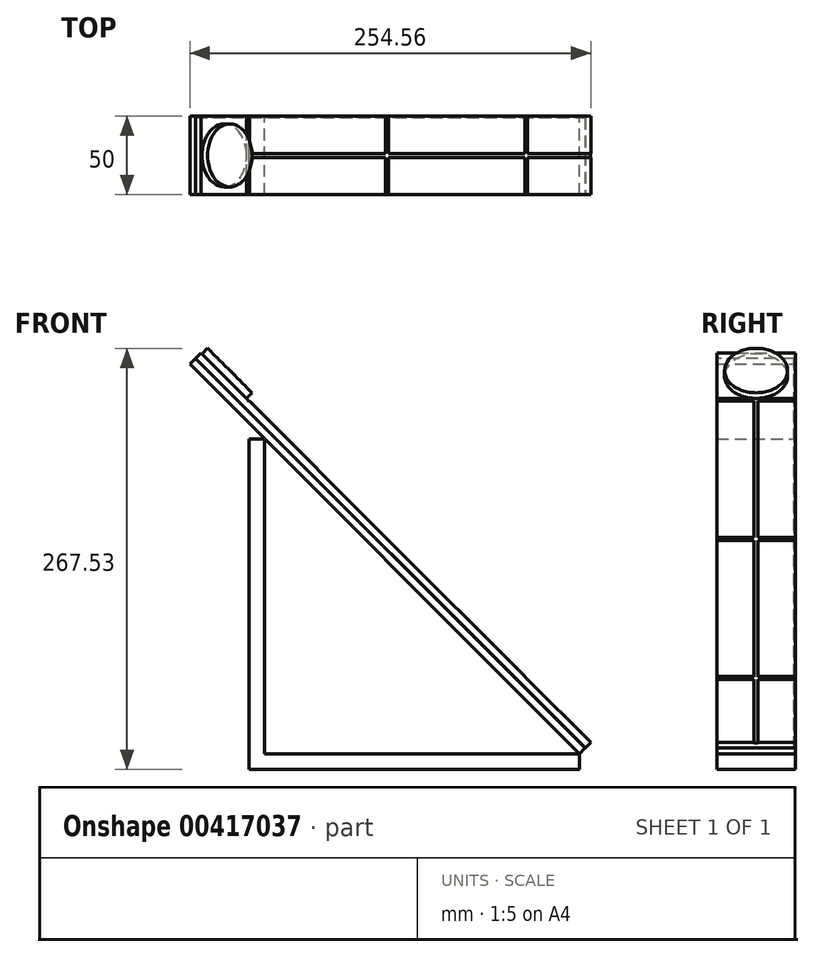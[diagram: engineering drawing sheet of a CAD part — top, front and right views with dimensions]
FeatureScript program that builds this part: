
annotation { "Feature Type Name" : "Feature", "Feature Type Description" : "" }
export const myFeature = defineFeature(function(context is Context, id is Id, definition is map)
    precondition{}
    {
        {
            var Q0;
            Q0=qCreatedBy(makeId("Top.planeOp"),FACE);
            var sketch = newSketch(context, id + "F0", { "sketchPlane" : qUnion([Q0])});
            skLineSegment(sketch, "E0.bottom", {"start": v(-52.98, -30.4) * mm, "end": v(147.02, -30.4) * mm});
            skLineSegment(sketch, "E0.top", {"start": v(-52.98, 19.6) * mm, "end": v(147.02, 19.6) * mm});
            skLineSegment(sketch, "E0.left", {"start": v(-52.98, -30.4) * mm, "end": v(-52.98, 19.6) * mm});
            skLineSegment(sketch, "E0.right", {"start": v(147.02, -30.4) * mm, "end": v(147.02, 19.6) * mm});
            skSolve(sketch);
        }
        {
            var Q0;
            Q0=makeQuery(id+"F0.imprint","IMPRINT",FACE,{"disambiguationData":[TD([[makeQuery(id+"F0.imprint","IMPRINT",EDGE,{"derivedFrom":sQuery(id+"F0.wireOp",EDGE,"E0.bottom")}),1.0]])]});
            extrude(context, id + "F1", {"entities" : qUnion([Q0]), "depth" : 200 * mm});
        }
        {
            var Q0;
            Q0=makeQuery(id+"F1.opExtrude","SWEPT_FACE",FACE,{"disambiguationData":[OSD([sQuery(id+"F0.wireOp",EDGE,"E0.bottom")])]});
            var sketch = newSketch(context, id + "F2", { "sketchPlane" : qUnion([Q0])});
            skLineSegment(sketch, "E1", {"start": v(-52.98, 200) * mm, "end": v(147.02, 0) * mm});
            skLineSegment(sketch, "E2", {"start": v(147.02, 0) * mm, "end": v(147.02, 200) * mm});
            skLineSegment(sketch, "E3", {"start": v(147.02, 200) * mm, "end": v(-52.98, 200) * mm});
            skSolve(sketch);
        }
        {
            var Q0;
            Q0=makeQuery(id+"F2.imprint","IMPRINT",FACE,{"disambiguationData":[TD([[makeQuery(id+"F2.imprint","IMPRINT",EDGE,{"derivedFrom":sQuery(id+"F2.wireOp",EDGE,"E1")}),1.0]])]});
            extrude(context, id + "F3", {"entities" : qUnion([Q0]), "operationType" : NewBodyOperationType.REMOVE, "oppositeDirection" : true, "depth" : 209 * mm});
        }
        {
            var Q0;
            Q0=makeQuery(id+"F3.boolean.opBoolean","COPY",FACE,{"derivedFrom":makeQuery(id+"F3.opExtrude","SWEPT_FACE",FACE,{"disambiguationData":[OSD([sQuery(id+"F2.wireOp",EDGE,"E1")])]})});
            var sketch = newSketch(context, id + "F4", { "sketchPlane" : qUnion([Q0])});
            skLineSegment(sketch, "E4.bottom", {"start": v(-30.4, -103.96) * mm, "end": v(19.6, -103.96) * mm});
            skLineSegment(sketch, "E4.top", {"start": v(-30.4, 246.04) * mm, "end": v(19.6, 246.04) * mm});
            skLineSegment(sketch, "E4.left", {"start": v(-30.4, -103.96) * mm, "end": v(-30.4, 246.04) * mm});
            skLineSegment(sketch, "E4.right", {"start": v(19.6, -103.96) * mm, "end": v(19.6, 246.04) * mm});
            skSolve(sketch);
        }
        {
            var Q0;
            {var subQ0=sQuery(id+"F4.wireOp",EDGE,"E4.top");Q0=makeQuery(id+"F4.imprint","IMPRINT",FACE,{"disambiguationData":[TD([[makeQuery(id+"F4.imprint","IMPRINT",EDGE,{"derivedFrom":subQ0}),-1.0]])]});}
            var Q1;
            {var subQ0=sQuery(id+"F4.wireOp",EDGE,"E4.bottom");Q1=makeQuery(id+"F4.imprint","IMPRINT",FACE,{"disambiguationData":[TD([[makeQuery(id+"F4.imprint","IMPRINT",EDGE,{"derivedFrom":subQ0}),1.0]])]});}
            extrude(context, id + "F5", {"entities" : qUnion([Q0, Q1]), "operationType" : NewBodyOperationType.ADD, "depth" : 10 * mm});
        }
        {
            var Q0;
            Q0=makeQuery(id+"F1.opExtrude","CAP_FACE",FACE,{"disambiguationData":[OSD([sQuery(id+"F0.wireOp",EDGE,"E0.bottom"),sQuery(id+"F0.wireOp",EDGE,"E0.top"),sQuery(id+"F0.wireOp",EDGE,"E0.left"),sQuery(id+"F0.wireOp",EDGE,"E0.right")])],"isStart":true});
            var sketch = newSketch(context, id + "F6", { "sketchPlane" : qUnion([Q0])});
            skLineSegment(sketch, "E5.bottom", {"start": v(147.02, 30.4) * mm, "end": v(-62.98, 30.4) * mm});
            skLineSegment(sketch, "E5.top", {"start": v(147.02, -19.6) * mm, "end": v(-62.98, -19.6) * mm});
            skLineSegment(sketch, "E5.left", {"start": v(147.02, 30.4) * mm, "end": v(147.02, -19.6) * mm});
            skLineSegment(sketch, "E5.right", {"start": v(-62.98, 30.4) * mm, "end": v(-62.98, -19.6) * mm});
            skSolve(sketch);
        }
        {
            var Q0;
            {var subQ2=sQuery(id+"F6.wireOp",EDGE,"E5.left");Q0=makeQuery(id+"F6.imprint","IMPRINT",FACE,{"disambiguationData":[TD([[makeQuery(id+"F6.imprint","IMPRINT",EDGE,{"derivedFrom":subQ2}),-1.0]])]});}
            var Q1;
            {var subQ2=sQuery(id+"F6.wireOp",EDGE,"E5.right");Q1=makeQuery(id+"F6.imprint","IMPRINT",FACE,{"disambiguationData":[TD([[makeQuery(id+"F6.imprint","IMPRINT",EDGE,{"derivedFrom":subQ2}),1.0]])]});}
            extrude(context, id + "F7", {"entities" : qUnion([Q0, Q1]), "operationType" : NewBodyOperationType.ADD, "depth" : 10 * mm});
        }
        {
            var Q0;
            Q0=makeQuery(id+"F1.opExtrude","SWEPT_FACE",FACE,{"disambiguationData":[OSD([sQuery(id+"F0.wireOp",EDGE,"E0.left")])]});
            var sketch = newSketch(context, id + "F8", { "sketchPlane" : qUnion([Q0])});
            skLineSegment(sketch, "E6.bottom", {"start": v(-19.6, 200) * mm, "end": v(30.4, 200) * mm});
            skLineSegment(sketch, "E6.top", {"start": v(-19.6, 0) * mm, "end": v(30.4, 0) * mm});
            skLineSegment(sketch, "E6.left", {"start": v(-19.6, 200) * mm, "end": v(-19.6, 0) * mm});
            skLineSegment(sketch, "E6.right", {"start": v(30.4, 200) * mm, "end": v(30.4, 0) * mm});
            skSolve(sketch);
        }
        {
            var Q0;
            Q0=makeQuery(id+"F8.imprint","IMPRINT",FACE,{"disambiguationData":[TD([[makeQuery(id+"F8.imprint","IMPRINT",EDGE,{"derivedFrom":sQuery(id+"F8.wireOp",EDGE,"E6.bottom")}),1.0]])]});
            extrude(context, id + "F9", {"entities" : qUnion([Q0]), "operationType" : NewBodyOperationType.ADD, "depth" : 10 * mm});
        }
        {
            var Q0;
            Q0=makeQuery(id+"F9.boolean.opBoolean","MERGE",FACE,{"derivedFrom":[makeQuery(id+"F7.boolean.opBoolean","MERGE",FACE,{"derivedFrom":[makeQuery(id+"F5.boolean.opBoolean","MERGE",FACE,{"derivedFrom":[makeQuery(id+"F1.opExtrude","SWEPT_FACE",FACE,{"disambiguationData":[OSD([sQuery(id+"F0.wireOp",EDGE,"E0.bottom")])]}),makeQuery(id+"F5.opExtrude","SWEPT_FACE",FACE,{"disambiguationData":[OSD([sQuery(id+"F4.wireOp",EDGE,"E4.left")])]})]}),makeQuery(id+"F7.opExtrude","SWEPT_FACE",FACE,{"disambiguationData":[OSD([sQuery(id+"F6.wireOp",EDGE,"E5.bottom")])]})]}),makeQuery(id+"F9.opExtrude","SWEPT_FACE",FACE,{"disambiguationData":[OSD([sQuery(id+"F8.wireOp",EDGE,"E6.right")])]})]});
            var sketch = newSketch(context, id + "F10", { "sketchPlane" : qUnion([Q0])});
            skLineSegment(sketch, "E7", {"start": v(-52.98, 200) * mm, "end": v(147.02, 0) * mm});
            skLineSegment(sketch, "E8", {"start": v(147.02, 0) * mm, "end": v(-52.98, 0) * mm});
            skLineSegment(sketch, "E9", {"start": v(-52.98, 0) * mm, "end": v(-52.98, 200) * mm});
            skSolve(sketch);
        }
        {
            var Q0;
            Q0=makeQuery(id+"F10.imprint","IMPRINT",FACE,{"disambiguationData":[TD([[makeQuery(id+"F10.imprint","IMPRINT",EDGE,{"derivedFrom":sQuery(id+"F10.wireOp",EDGE,"E7")}),-1.0]])]});
            extrude(context, id + "F11", {"entities" : qUnion([Q0]), "operationType" : NewBodyOperationType.REMOVE, "oppositeDirection" : true, "depth" : 234.7 * mm});
        }
        {
            var Q0;
            Q0=makeQuery(id+"F5.opExtrude","CAP_FACE",FACE,{"disambiguationData":[OSD([sQuery(id+"F4.wireOp",EDGE,"E4.bottom"),sQuery(id+"F4.wireOp",EDGE,"E4.top"),sQuery(id+"F4.wireOp",EDGE,"E4.left"),sQuery(id+"F4.wireOp",EDGE,"E4.right")])],"isStart":false});
            var sketch = newSketch(context, id + "F12", { "sketchPlane" : qUnion([Q0])});
            skLineSegment(sketch, "E10.bottom", {"start": v(-30.4, 205.25) * mm, "end": v(19.6, 205.25) * mm});
            skLineSegment(sketch, "E10.top", {"start": v(-30.4, 202.75) * mm, "end": v(19.6, 202.75) * mm});
            skLineSegment(sketch, "E10.left", {"start": v(-30.4, 205.25) * mm, "end": v(-30.4, 202.75) * mm});
            skLineSegment(sketch, "E10.right", {"start": v(19.6, 205.25) * mm, "end": v(19.6, 202.75) * mm});
            skLineSegment(sketch, "E11.bottom", {"start": v(-30.4, -47.25) * mm, "end": v(19.6, -47.25) * mm});
            skLineSegment(sketch, "E11.top", {"start": v(-30.4, -44.75) * mm, "end": v(19.6, -44.75) * mm});
            skLineSegment(sketch, "E11.left", {"start": v(-30.4, -47.25) * mm, "end": v(-30.4, -44.75) * mm});
            skLineSegment(sketch, "E11.right", {"start": v(19.6, -47.25) * mm, "end": v(19.6, -44.75) * mm});
            skLineSegment(sketch, "E12.bottom", {"start": v(-30.4, 77.75) * mm, "end": v(19.6, 77.75) * mm});
            skLineSegment(sketch, "E12.top", {"start": v(-30.4, 80.25) * mm, "end": v(19.6, 80.25) * mm});
            skLineSegment(sketch, "E12.left", {"start": v(-30.4, 77.75) * mm, "end": v(-30.4, 80.25) * mm});
            skLineSegment(sketch, "E12.right", {"start": v(19.6, 77.75) * mm, "end": v(19.6, 80.25) * mm});
            skLineSegment(sketch, "E13.bottom", {"start": v(-6.65, 246.04) * mm, "end": v(-4.15, 246.04) * mm});
            skLineSegment(sketch, "E13.left", {"start": v(-6.65, 246.04) * mm, "end": v(-6.65, -103.96) * mm});
            skLineSegment(sketch, "E13.right", {"start": v(-4.15, 246.04) * mm, "end": v(-4.15, -103.96) * mm});
            skLineSegment(sketch, "E14", {"start": v(-6.65, -103.96) * mm, "end": v(-4.15, -103.96) * mm});
            skSolve(sketch);
        }
        {
            var Q0;
            Q0=makeQuery(id+"F12.imprint","IMPRINT",FACE,{"disambiguationData":[TD([[makeQuery(id+"F12.imprint","IMPRINT",EDGE,{"derivedFrom":sQuery(id+"F12.wireOp",EDGE,"E10.bottom")}),-1.0]])]});
            var Q1;
            Q1=makeQuery(id+"F12.imprint","IMPRINT",FACE,{"disambiguationData":[TD([[makeQuery(id+"F12.imprint","IMPRINT",EDGE,{"derivedFrom":sQuery(id+"F12.wireOp",EDGE,"E11.bottom")}),1.0]])]});
            var Q2;
            Q2=makeQuery(id+"F12.imprint","IMPRINT",FACE,{"disambiguationData":[TD([[makeQuery(id+"F12.imprint","IMPRINT",EDGE,{"derivedFrom":sQuery(id+"F12.wireOp",EDGE,"E12.bottom")}),1.0]])]});
            var Q3;
            {var subQ0=sQuery(id+"F12.wireOp",EDGE,"E13.left");var subQ1=sQuery(id+"F12.wireOp",EDGE,"E10.top");var subQ2=makeQuery(id+"F12.imprint","INTERSECT",VERTEX,{"derivedFrom":[subQ1,subQ0]});Q3=makeQuery(id+"F12.imprint","IMPRINT",FACE,{"disambiguationData":[TD([[makeQuery(id+"F12.imprint","IMPRINT",EDGE,{"disambiguationData":[TD([[subQ2,-1.0]])],"derivedFrom":subQ1}),-1.0]])]});}
            var Q4;
            {var subQ0=sQuery(id+"F12.wireOp",EDGE,"E13.left");var subQ1=sQuery(id+"F12.wireOp",EDGE,"E11.top");var subQ2=makeQuery(id+"F12.imprint","INTERSECT",VERTEX,{"derivedFrom":[subQ1,subQ0]});Q4=makeQuery(id+"F12.imprint","IMPRINT",FACE,{"disambiguationData":[TD([[makeQuery(id+"F12.imprint","IMPRINT",EDGE,{"disambiguationData":[TD([[subQ2,-1.0]])],"derivedFrom":subQ1}),1.0]])]});}
            var Q5;
            {var subQ5=sQuery(id+"F12.wireOp",EDGE,"E14");Q5=makeQuery(id+"F12.imprint","IMPRINT",FACE,{"disambiguationData":[TD([[makeQuery(id+"F12.imprint","IMPRINT",EDGE,{"derivedFrom":subQ5}),1.0]])]});}
            extrude(context, id + "F13", {"entities" : qUnion([Q0, Q1, Q2, Q3, Q4, Q5]), "operationType" : NewBodyOperationType.REMOVE, "oppositeDirection" : true, "depth" : 0.1 * mm, "offsetDistance" : 25 * mm});
        }
        {
            var Q0;
            {var subQ0=sQuery(id+"F4.wireOp",EDGE,"E4.left");var subQ1=sQuery(id+"F4.wireOp",EDGE,"E4.top");var subQ2=sQuery(id+"F4.wireOp",EDGE,"E4.right");Q0=makeQuery(id+"F13.boolean.opBoolean","SPLIT",FACE,{"disambiguationData":[TD([makeQuery(id+"F5.opExtrude","SWEPT_FACE",FACE,{"disambiguationData":[OSD([subQ1])]})])],"derivedFrom":makeQuery(id+"F5.opExtrude","CAP_FACE",FACE,{"disambiguationData":[OSD([sQuery(id+"F4.wireOp",EDGE,"E4.bottom"),subQ1,subQ0,subQ2])],"isStart":false})});}
            var sketch = newSketch(context, id + "F14", { "sketchPlane" : qUnion([Q0])});
            skCircle(sketch, "E15", {"center": v(-5.4, 225.25) * mm, "radius": 20 * mm});
            skSolve(sketch);
        }
        {
            var Q0;
            Q0=makeQuery(id+"F14.imprint","IMPRINT",FACE,{"disambiguationData":[TD([[makeQuery(id+"F14.imprint","IMPRINT",EDGE,{"derivedFrom":sQuery(id+"F14.wireOp",EDGE,"E15")}),1.0]])]});
            extrude(context, id + "F15", {"entities" : qUnion([Q0]), "operationType" : NewBodyOperationType.ADD, "depth" : 5 * mm});
        }
        {
            var Q0;
            {var subQ2=sQuery(id+"F4.wireOp",EDGE,"E4.left");var subQ3=sQuery(id+"F4.wireOp",EDGE,"E4.bottom");Q0=makeQuery(id+"F11.boolean.opBoolean","SPLIT",FACE,{"disambiguationData":[TD([makeQuery(id+"F5.opExtrude","SWEPT_FACE",FACE,{"disambiguationData":[OSD([subQ3])]})])],"derivedFrom":makeQuery(id+"F9.boolean.opBoolean","MERGE",FACE,{"derivedFrom":[makeQuery(id+"F7.boolean.opBoolean","MERGE",FACE,{"derivedFrom":[makeQuery(id+"F5.boolean.opBoolean","MERGE",FACE,{"derivedFrom":[makeQuery(id+"F1.opExtrude","SWEPT_FACE",FACE,{"disambiguationData":[OSD([sQuery(id+"F0.wireOp",EDGE,"E0.bottom")])]}),makeQuery(id+"F5.opExtrude","SWEPT_FACE",FACE,{"disambiguationData":[OSD([subQ2])]})]}),makeQuery(id+"F7.opExtrude","SWEPT_FACE",FACE,{"disambiguationData":[OSD([sQuery(id+"F6.wireOp",EDGE,"E5.bottom")])]})]}),makeQuery(id+"F9.opExtrude","SWEPT_FACE",FACE,{"disambiguationData":[OSD([sQuery(id+"F8.wireOp",EDGE,"E6.right")])]})]})});}
            var sketch = newSketch(context, id + "F16", { "sketchPlane" : qUnion([Q0])});
            skLineSegment(sketch, "E16", {"start": v(-96.94, 251.02) * mm, "end": v(150.55, 3.54) * mm});
            skLineSegment(sketch, "E17", {"start": v(150.55, 3.54) * mm, "end": v(150.62, 3.6) * mm});
            skLineSegment(sketch, "E18", {"start": v(150.62, 3.6) * mm, "end": v(-96.87, 251.1) * mm});
            skLineSegment(sketch, "E19", {"start": v(-96.87, 251.1) * mm, "end": v(-96.94, 251.02) * mm});
            skSolve(sketch);
        }
        {
            var Q0;
            Q0=makeQuery(id+"F16.imprint","IMPRINT",FACE,{"disambiguationData":[TD([[makeQuery(id+"F16.imprint","IMPRINT",EDGE,{"derivedFrom":sQuery(id+"F16.wireOp",EDGE,"E16")}),1.0]])]});
            extrude(context, id + "F17", {"entities" : qUnion([Q0]), "operationType" : NewBodyOperationType.REMOVE, "oppositeDirection" : true, "depth" : 49 * mm});
        }
    });
